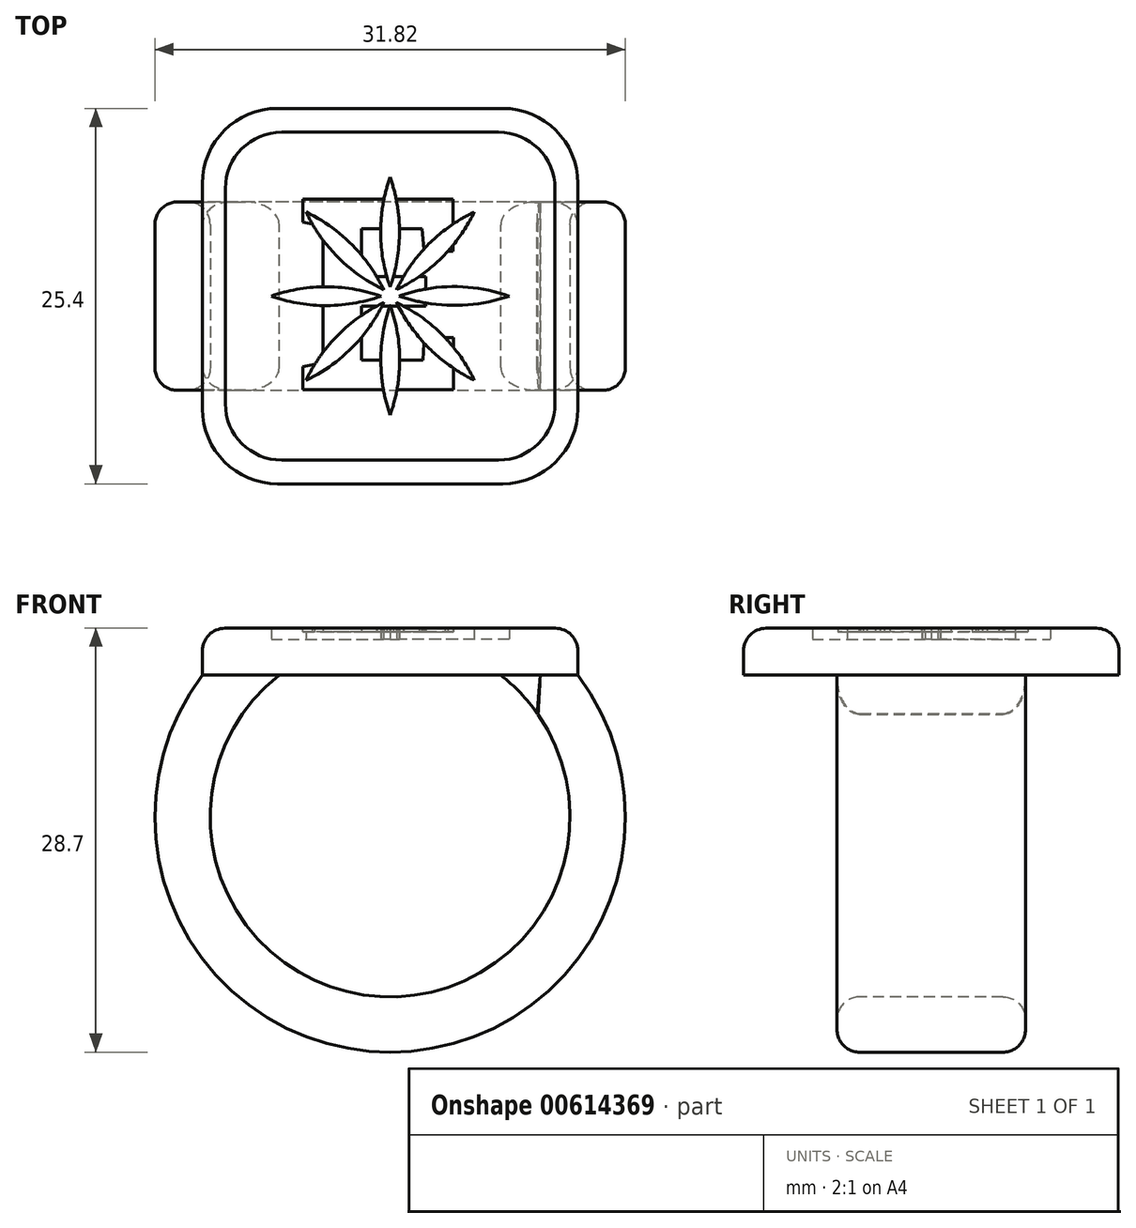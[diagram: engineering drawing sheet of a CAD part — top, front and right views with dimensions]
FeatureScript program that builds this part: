
annotation { "Feature Type Name" : "Feature", "Feature Type Description" : "" }
export const myFeature = defineFeature(function(context is Context, id is Id, definition is map)
    precondition{}
    {
        {
            var Q0;
            Q0=qCreatedBy(makeId("Top.planeOp"),FACE);
            var sketch = newSketch(context, id + "F0", { "sketchPlane" : qUnion([Q0])});
            skLineSegment(sketch, "E0.bottom", {"start": v(-12.7, 12.7) * mm, "end": v(12.7, 12.7) * mm});
            skLineSegment(sketch, "E0.top", {"start": v(-12.7, -12.7) * mm, "end": v(12.7, -12.7) * mm});
            skLineSegment(sketch, "E0.left", {"start": v(-12.7, 12.7) * mm, "end": v(-12.7, -12.7) * mm});
            skLineSegment(sketch, "E0.right", {"start": v(12.7, 12.7) * mm, "end": v(12.7, -12.7) * mm});
            skPoint(sketch, "E0.middle", {"position": v(0, 0) * mm});
            skSolve(sketch);
        }
        {
            var Q0;
            Q0=qSketchRegion(id+"F0",true);
            extrude(context, id + "F1", {"entities" : qUnion([Q0]), "depth" : 3.17 * mm, "offsetDistance" : 25.4 * mm});
        }
        {
            var Q0;
            Q0=qCreatedBy(makeId("Front.planeOp"),FACE);
            var sketch = newSketch(context, id + "F2", { "sketchPlane" : qUnion([Q0])});
            skArc(sketch, "E1", {"start": v(-10.16, 0) * mm, "mid": v(0, -23.56) * mm, "end": v(10.16, 0) * mm});
            skSolve(sketch);
        }
        {
            var Q0;
            Q0=makeQuery(id+"F1.opExtrude","CAP_FACE",FACE,{"disambiguationData":[OSD([sQuery(id+"F0.wireOp",EDGE,"E0.bottom"),sQuery(id+"F0.wireOp",EDGE,"E0.top"),sQuery(id+"F0.wireOp",EDGE,"E0.left"),sQuery(id+"F0.wireOp",EDGE,"E0.right")])],"isStart":true});
            var sketch = newSketch(context, id + "F3", { "sketchPlane" : qUnion([Q0])});
            skLineSegment(sketch, "E2.bottom", {"start": v(-12.7, 6.38) * mm, "end": v(-7.5, 6.38) * mm});
            skLineSegment(sketch, "E2.top", {"start": v(-12.7, -6.38) * mm, "end": v(-7.5, -6.38) * mm});
            skLineSegment(sketch, "E2.left", {"start": v(-12.7, 6.38) * mm, "end": v(-12.7, -6.38) * mm});
            skLineSegment(sketch, "E2.right", {"start": v(-7.5, 6.38) * mm, "end": v(-7.5, -6.38) * mm});
            skPoint(sketch, "E2.middle", {"position": v(-10.1, 0) * mm});
            skPoint(sketch, "E2.middle.positionSnap0", {"position": v(-12.7, 0) * mm});
            skPoint(sketch, "E2.centerSnap0", {"position": v(-12.7, 0) * mm});
            skSolve(sketch);
        }
        {
            var Q0;
            Q0=makeQuery(id+"F3.imprint","IMPRINT",FACE,{"disambiguationData":[TD([[makeQuery(id+"F3.imprint","IMPRINT",EDGE,{"derivedFrom":sQuery(id+"F3.wireOp",EDGE,"E2.bottom")}),-1.0]])]});
            var Q1;
            Q1=sQuery(id+"F2.wireOp",EDGE,"E1");
            sweep(context, id + "F4", {"operationType" : NewBodyOperationType.ADD, "profiles" : qUnion([Q0]), "path" : qUnion([Q1])});
        }
        {
            var Q0;
            Q0=qCreatedBy(makeId("Front.planeOp"),FACE);
            var sketch = newSketch(context, id + "F5", { "sketchPlane" : qUnion([Q0])});
            skLineSegment(sketch, "E3", {"start": v(-7.47, 0) * mm, "end": v(0, 0) * mm});
            skLineSegment(sketch, "E4", {"start": v(0, 0) * mm, "end": v(7.49, 0) * mm});
            skArc(sketch, "E5", {"start": v(9.95, -2.58) * mm, "mid": v(8.81, -1.2) * mm, "end": v(7.49, 0) * mm});
            skLineSegment(sketch, "E6", {"start": v(7.49, 0) * mm, "end": v(10.16, 0) * mm});
            skLineSegment(sketch, "E7", {"start": v(10.16, 0) * mm, "end": v(9.95, -2.58) * mm});
            skSolve(sketch);
        }
        {
            var Q0;
            Q0=qSketchRegion(id+"F5",true);
            extrude(context, id + "F6", {"entities" : qUnion([Q0]), "operationType" : NewBodyOperationType.ADD, "depth" : 12.7 * mm, "offsetDistance" : 25.4 * mm, "symmetric" : true});
        }
        {
            var Q0;
            Q0=makeQuery(id+"F1.opExtrude","SWEPT_EDGE",EDGE,{"disambiguationData":[OSD([sQuery(id+"F0.wireOp",EDGE,"E0.top"),sQuery(id+"F0.wireOp",EDGE,"E0.right")])]});
            var Q1;
            Q1=makeQuery(id+"F1.opExtrude","SWEPT_EDGE",EDGE,{"disambiguationData":[OSD([sQuery(id+"F0.wireOp",EDGE,"E0.top"),sQuery(id+"F0.wireOp",EDGE,"E0.left")])]});
            var Q2;
            Q2=makeQuery(id+"F1.opExtrude","SWEPT_EDGE",EDGE,{"disambiguationData":[OSD([sQuery(id+"F0.wireOp",EDGE,"E0.bottom"),sQuery(id+"F0.wireOp",EDGE,"E0.left")])]});
            var Q3;
            Q3=makeQuery(id+"F1.opExtrude","SWEPT_EDGE",EDGE,{"disambiguationData":[OSD([sQuery(id+"F0.wireOp",EDGE,"E0.bottom"),sQuery(id+"F0.wireOp",EDGE,"E0.right")])]});
            fillet(context, id + "F7", {"entities" : qUnion([Q0, Q1, Q2, Q3]), "radius" : 5.08 * mm, "tangentPropagation" : true, "allowEdgeOverflow" : false});
        }
        {
            var Q0;
            Q0=makeQuery(id+"F4.opSweep","SWEPT_EDGE",EDGE,{"disambiguationData":[OSD([sQuery(id+"F2.wireOp",EDGE,"E1"),sQuery(id+"F3.wireOp",EDGE,"E2.top"),sQuery(id+"F3.wireOp",EDGE,"E2.right")])]});
            var Q1;
            Q1=makeQuery(id+"F4.opSweep","SWEPT_EDGE",EDGE,{"disambiguationData":[OSD([sQuery(id+"F0.wireOp",EDGE,"E0.left"),sQuery(id+"F2.wireOp",EDGE,"E1"),sQuery(id+"F3.wireOp",EDGE,"E2.top"),sQuery(id+"F3.wireOp",EDGE,"E2.left")])]});
            var Q2;
            Q2=makeQuery(id+"F4.opSweep","SWEPT_EDGE",EDGE,{"disambiguationData":[OSD([sQuery(id+"F0.wireOp",EDGE,"E0.left"),sQuery(id+"F2.wireOp",EDGE,"E1"),sQuery(id+"F3.wireOp",EDGE,"E2.bottom"),sQuery(id+"F3.wireOp",EDGE,"E2.left")])]});
            var Q3;
            Q3=makeQuery(id+"F4.opSweep","SWEPT_EDGE",EDGE,{"disambiguationData":[OSD([sQuery(id+"F2.wireOp",EDGE,"E1"),sQuery(id+"F3.wireOp",EDGE,"E2.bottom"),sQuery(id+"F3.wireOp",EDGE,"E2.right")])]});
            fillet(context, id + "F8", {"entities" : qUnion([Q0, Q1, Q2, Q3]), "radius" : 1.52 * mm, "tangentPropagation" : true, "allowEdgeOverflow" : false});
        }
        {
            var Q0;
            Q0=makeQuery(id+"F1.opExtrude","CAP_FACE",FACE,{"disambiguationData":[OSD([sQuery(id+"F0.wireOp",EDGE,"E0.bottom"),sQuery(id+"F0.wireOp",EDGE,"E0.top"),sQuery(id+"F0.wireOp",EDGE,"E0.left"),sQuery(id+"F0.wireOp",EDGE,"E0.right")])],"isStart":false});
            fillet(context, id + "F9", {"entities" : qUnion([Q0]), "radius" : 1.52 * mm, "tangentPropagation" : true, "allowEdgeOverflow" : false});
        }
        {
            var Q0;
            Q0=makeQuery(id+"F1.opExtrude","CAP_FACE",FACE,{"disambiguationData":[OSD([sQuery(id+"F0.wireOp",EDGE,"E0.bottom"),sQuery(id+"F0.wireOp",EDGE,"E0.top"),sQuery(id+"F0.wireOp",EDGE,"E0.left"),sQuery(id+"F0.wireOp",EDGE,"E0.right")])],"isStart":false});
            var sketch = newSketch(context, id + "F10", { "sketchPlane" : qUnion([Q0])});
            skLineSegment(sketch, "E8.bottom", {"start": v(-11.15, 11.1) * mm, "end": v(11.15, 11.1) * mm});
            skLineSegment(sketch, "E8.top", {"start": v(-11.15, -11.1) * mm, "end": v(11.15, -11.1) * mm});
            skLineSegment(sketch, "E8.left", {"start": v(-11.15, 11.1) * mm, "end": v(-11.15, -11.1) * mm});
            skLineSegment(sketch, "E8.right", {"start": v(11.15, 11.1) * mm, "end": v(11.15, -11.1) * mm});
            skPoint(sketch, "E8.middle", {"position": v(0, 0) * mm});
            skSolve(sketch);
        }
        {
            var Q0;
            Q0=qSketchRegion(id+"F10",true);
            extrude(context, id + "F11", {"entities" : qUnion([Q0]), "operationType" : NewBodyOperationType.ADD, "depth" : 0.03 * mm, "offsetDistance" : 25.4 * mm});
        }
        {
            var Q0;
            Q0=makeQuery(id+"F11.opExtrude","SWEPT_EDGE",EDGE,{"disambiguationData":[OSD([sQuery(id+"F10.wireOp",EDGE,"E8.bottom"),sQuery(id+"F10.wireOp",EDGE,"E8.left")])]});
            var Q1;
            Q1=makeQuery(id+"F11.opExtrude","SWEPT_EDGE",EDGE,{"disambiguationData":[OSD([sQuery(id+"F10.wireOp",EDGE,"E8.bottom"),sQuery(id+"F10.wireOp",EDGE,"E8.right")])]});
            var Q2;
            Q2=makeQuery(id+"F11.opExtrude","SWEPT_EDGE",EDGE,{"disambiguationData":[OSD([sQuery(id+"F10.wireOp",EDGE,"E8.top"),sQuery(id+"F10.wireOp",EDGE,"E8.right")])]});
            var Q3;
            Q3=makeQuery(id+"F11.opExtrude","SWEPT_EDGE",EDGE,{"disambiguationData":[OSD([sQuery(id+"F10.wireOp",EDGE,"E8.top"),sQuery(id+"F10.wireOp",EDGE,"E8.left")])]});
            fillet(context, id + "F12", {"entities" : qUnion([Q0, Q1, Q2, Q3]), "radius" : 3.8 * mm, "tangentPropagation" : true, "allowEdgeOverflow" : false});
        }
        {
            var Q0;
            Q0=makeQuery(id+"F11.opExtrude","CAP_FACE",FACE,{"disambiguationData":[OSD([sQuery(id+"F10.wireOp",EDGE,"E8.bottom"),sQuery(id+"F10.wireOp",EDGE,"E8.top"),sQuery(id+"F10.wireOp",EDGE,"E8.left"),sQuery(id+"F10.wireOp",EDGE,"E8.right")])],"isStart":false});
            var sketch = newSketch(context, id + "F13", { "sketchPlane" : qUnion([Q0])});
            skArc(sketch, "E9", {"start": v(0, 8.05) * mm, "mid": v(-0.64, 4.33) * mm, "end": v(0, 0.6) * mm});
            skArc(sketch, "E10", {"start": v(0, 0.6) * mm, "mid": v(0.63, 4.33) * mm, "end": v(0, 8.05) * mm});
            skArc(sketch, "E11.1.0", {"start": v(-0.43, 0.43) * mm, "mid": v(-2.61, 3.5) * mm, "end": v(-5.7, 5.7) * mm});
            skArc(sketch, "E11.1.1", {"start": v(-5.7, 5.7) * mm, "mid": v(-3.52, 2.6) * mm, "end": v(-0.43, 0.43) * mm});
            skArc(sketch, "E11.2.0", {"start": v(-0.6, 0) * mm, "mid": v(-4.33, 0.63) * mm, "end": v(-8.05, 0) * mm});
            skArc(sketch, "E11.2.1", {"start": v(-8.05, 0) * mm, "mid": v(-4.33, -0.64) * mm, "end": v(-0.6, 0) * mm});
            skArc(sketch, "E11.3.0", {"start": v(-0.43, -0.43) * mm, "mid": v(-3.5, -2.61) * mm, "end": v(-5.7, -5.7) * mm});
            skArc(sketch, "E11.3.1", {"start": v(-5.7, -5.7) * mm, "mid": v(-2.6, -3.52) * mm, "end": v(-0.43, -0.43) * mm});
            skArc(sketch, "E11.4.0", {"start": v(0, -0.6) * mm, "mid": v(-0.63, -4.33) * mm, "end": v(0, -8.05) * mm});
            skArc(sketch, "E11.4.1", {"start": v(0, -8.05) * mm, "mid": v(0.64, -4.33) * mm, "end": v(0, -0.6) * mm});
            skArc(sketch, "E11.5.0", {"start": v(0.43, -0.43) * mm, "mid": v(2.61, -3.5) * mm, "end": v(5.7, -5.7) * mm});
            skArc(sketch, "E11.5.1", {"start": v(5.7, -5.7) * mm, "mid": v(3.52, -2.6) * mm, "end": v(0.43, -0.43) * mm});
            skArc(sketch, "E11.6.0", {"start": v(0.6, 0) * mm, "mid": v(4.33, -0.63) * mm, "end": v(8.05, 0) * mm});
            skArc(sketch, "E11.6.1", {"start": v(8.05, 0) * mm, "mid": v(4.33, 0.64) * mm, "end": v(0.6, 0) * mm});
            skArc(sketch, "E11.7.0", {"start": v(0.43, 0.43) * mm, "mid": v(3.5, 2.61) * mm, "end": v(5.7, 5.7) * mm});
            skArc(sketch, "E11.7.1", {"start": v(5.7, 5.7) * mm, "mid": v(2.6, 3.52) * mm, "end": v(0.43, 0.43) * mm});
            skPoint(sketch, "E11.center", {"position": v(0, 0) * mm});
            skSolve(sketch);
        }
        {
            var Q0;
            Q0=qSketchRegion(id+"F13",true);
            extrude(context, id + "F14", {"entities" : qUnion([Q0]), "operationType" : NewBodyOperationType.REMOVE, "depth" : 1.52 * mm, "offsetDistance" : 25.4 * mm, "symmetric" : true});
        }
        {
            var Q0;
            Q0=makeQuery(id+"F11.opExtrude","CAP_FACE",FACE,{"disambiguationData":[OSD([sQuery(id+"F10.wireOp",EDGE,"E8.bottom"),sQuery(id+"F10.wireOp",EDGE,"E8.top"),sQuery(id+"F10.wireOp",EDGE,"E8.left"),sQuery(id+"F10.wireOp",EDGE,"E8.right")])],"isStart":false});
            var sketch = newSketch(context, id + "F15", { "sketchPlane" : qUnion([Q0])});
            skText(sketch, "E12", { "text": "E", "fontName": "RobotoSlab-Bold.ttf"});
            const initialGuessF15  = {"E12": [-0.00639, -0.00632, 1, 0, 0.01303]};
            skSetInitialGuess(sketch, initialGuessF15);
            skSolve(sketch);
        }
        {
            var Q0;
            Q0=qSketchRegion(id+"F15",true);
            extrude(context, id + "F16", {"entities" : qUnion([Q0]), "operationType" : NewBodyOperationType.REMOVE, "oppositeDirection" : true, "depth" : 0.25 * mm, "offsetDistance" : 25.4 * mm});
        }
        {
            var Q0;
            Q0=makeQuery(id+"F6.opExtrude","CAP_EDGE",EDGE,{"disambiguationData":[OSD([sQuery(id+"F5.wireOp",EDGE,"E5")])],"isStart":false});
            var Q1;
            Q1=makeQuery(id+"F6.opExtrude","CAP_EDGE",EDGE,{"disambiguationData":[OSD([sQuery(id+"F5.wireOp",EDGE,"E5")])],"isStart":true});
            fillet(context, id + "F17", {"entities" : qUnion([Q0, Q1]), "radius" : 1.52 * mm, "tangentPropagation" : true, "allowEdgeOverflow" : false});
        }
    });
